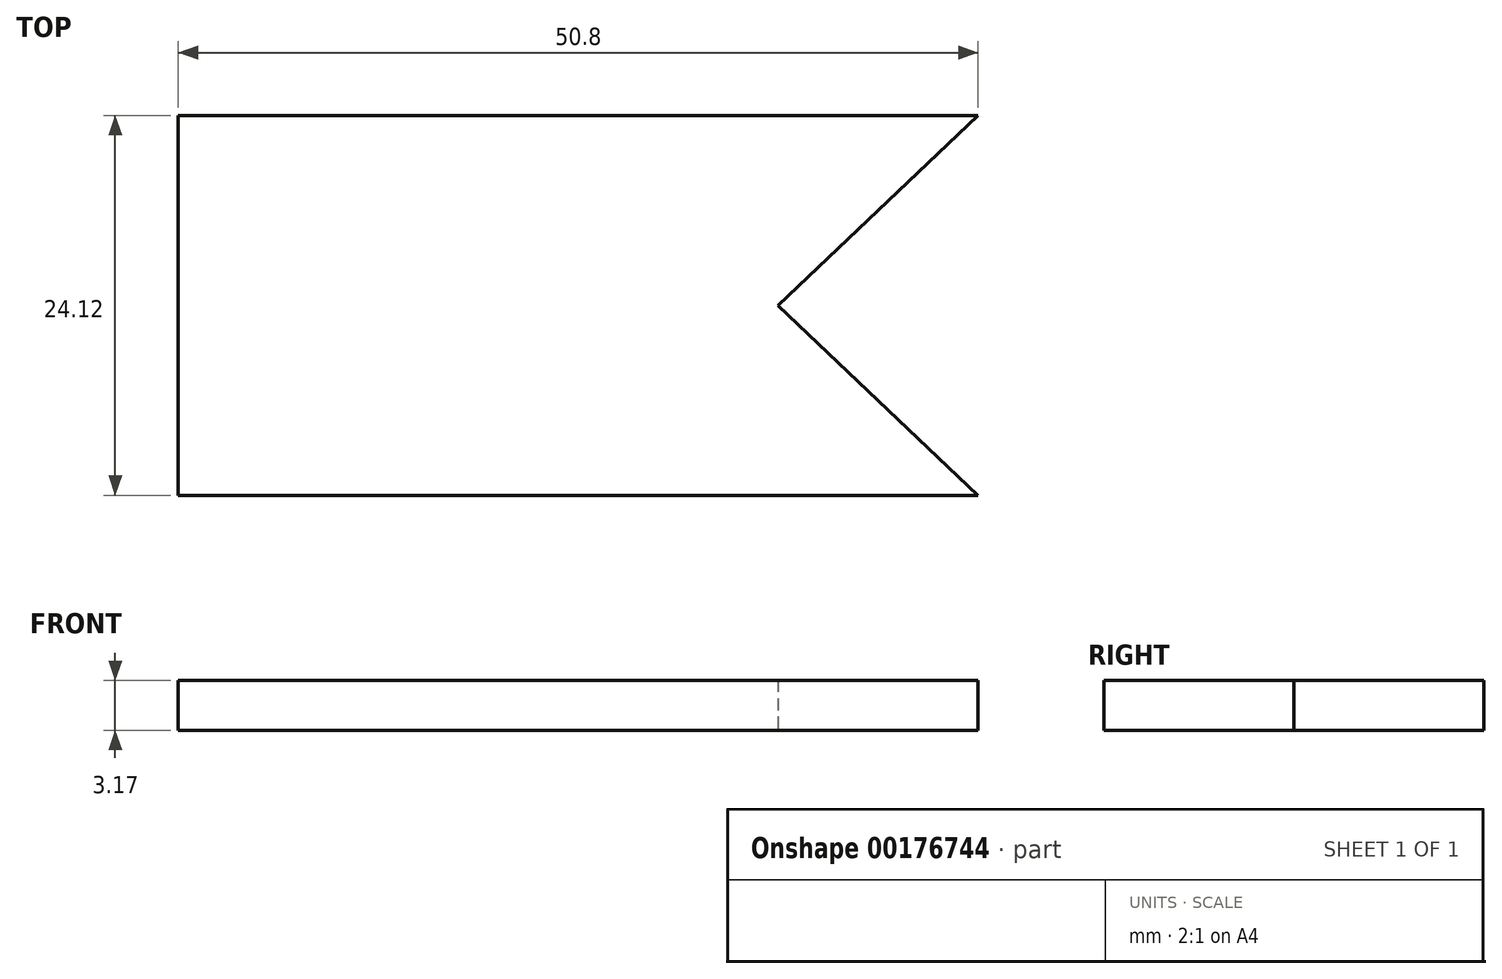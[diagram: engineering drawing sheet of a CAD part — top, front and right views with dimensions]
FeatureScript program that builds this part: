
annotation { "Feature Type Name" : "Feature", "Feature Type Description" : "" }
export const myFeature = defineFeature(function(context is Context, id is Id, definition is map)
    precondition{}
    {
        {
            var Q0;
            Q0=qCreatedBy(makeId("Top.planeOp"),FACE);
            var sketch = newSketch(context, id + "F0", { "sketchPlane" : qUnion([Q0])});
            skLineSegment(sketch, "E0.bottom", {"start": v(-25.4, 12.07) * mm, "end": v(25.4, 12.07) * mm});
            skLineSegment(sketch, "E0.top", {"start": v(-25.4, -12.06) * mm, "end": v(25.4, -12.06) * mm});
            skLineSegment(sketch, "E0.left", {"start": v(-25.4, 12.06) * mm, "end": v(-25.4, -12.06) * mm});
            skLineSegment(sketch, "E0.right", {"start": v(25.4, 12.07) * mm, "end": v(25.4, -12.06) * mm, "construction": true});
            skLineSegment(sketch, "E1", {"start": v(-25.4, 12.07) * mm, "end": v(25.4, -12.06) * mm, "construction": true});
            skLineSegment(sketch, "E2", {"start": v(25.4, 12.07) * mm, "end": v(12.7, 0) * mm});
            skLineSegment(sketch, "E3", {"start": v(12.7, 0) * mm, "end": v(25.4, -12.07) * mm});
            skSolve(sketch);
        }
        {
            var Q0;
            Q0 = qSketchRegion(id + "F0", true);
            extrude(context, id + "F1", {"entities" : qUnion([Q0]), "depth" : 3.17 * mm});
        }
    });
